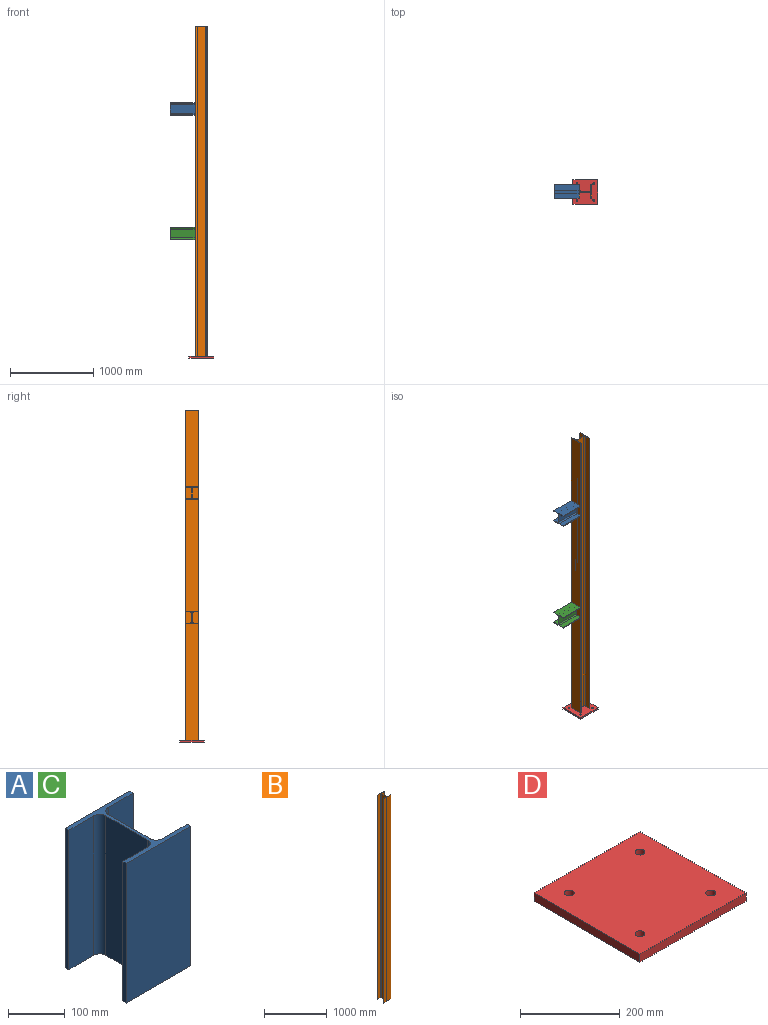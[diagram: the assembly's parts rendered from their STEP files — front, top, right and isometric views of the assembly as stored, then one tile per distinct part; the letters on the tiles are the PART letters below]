
ASSEMBLY  parts=4 mates=2
PART A: 18 faces, bbox 160x152x300 mm
  f0: plane 300x9mm, normal (-1,0,0), area 2700mm2, adj f1,f15,f16,f17
  f1: plane 300x62mm, normal (0,1,0), area 18600mm2, adj f0,f2,f16,f17
  f2: cylinder r=15mm len=300mm, axis (0,0,1), area 7068.6mm2, adj f1,f3,f16,f17
  f3: plane 300x104mm, normal (-1,0,0), area 31200mm2, adj f2,f4,f16,f17
  f4: cylinder r=15mm len=300mm, axis (0,0,1), area 7068.6mm2, adj f3,f5,f16,f17
  f5: plane 300x62mm, normal (0,-1,0), area 18600mm2, adj f4,f6,f16,f17
  f6: plane 300x9mm, normal (-1,0,0), area 2700mm2, adj f5,f7,f16,f17
  f7: plane 300x160mm, normal (0,1,0), area 48000mm2, adj f6,f8,f16,f17
  f8: plane 300x9mm, normal (1,0,0), area 2700mm2, adj f7,f9,f16,f17
  f9: plane 300x62mm, normal (0,-1,0), area 18600mm2, adj f8,f10,f16,f17
  f10: cylinder r=15mm len=300mm, axis (0,0,1), area 7068.6mm2, adj f9,f11,f16,f17
  f11: plane 300x104mm, normal (1,0,0), area 31200mm2, adj f10,f12,f16,f17
  f12: cylinder r=15mm len=300mm, axis (0,0,1), area 7068.6mm2, adj f11,f13,f16,f17
  f13: plane 300x62mm, normal (0,1,0), area 18600mm2, adj f12,f14,f16,f17
  f14: plane 300x9mm, normal (1,0,0), area 2700mm2, adj f13,f15,f16,f17
  f15: plane 300x160mm, normal (0,-1,0), area 48000mm2, adj f0,f14,f16,f17
  f16: plane 160x152mm, normal (0,0,1), area 3877.1mm2, adj f0,f1,f2,f3,f4,f5,f6,f7
  f17: plane 160x152mm, normal (0,0,-1), area 3877.1mm2, adj f0,f1,f2,f3,f4,f5,f6,f7
PART B: 18 faces, bbox 160x152x3980 mm
  f0: plane 3980x9mm, normal (-1,0,0), area 35820mm2, adj f1,f15,f16,f17
  f1: plane 3980x62mm, normal (0,1,0), area 246760mm2, adj f0,f2,f16,f17
  f2: cylinder r=15mm len=3980mm, axis (0,0,1), area 93776.5mm2, adj f1,f3,f16,f17
  f3: plane 3980x104mm, normal (-1,0,0), area 413920mm2, adj f2,f4,f16,f17
  f4: cylinder r=15mm len=3980mm, axis (0,0,1), area 93776.5mm2, adj f3,f5,f16,f17
  f5: plane 3980x62mm, normal (0,-1,0), area 246760mm2, adj f4,f6,f16,f17
  f6: plane 3980x9mm, normal (-1,0,0), area 35820mm2, adj f5,f7,f16,f17
  f7: plane 3980x160mm, normal (0,1,0), area 636800mm2, adj f6,f8,f16,f17
  f8: plane 3980x9mm, normal (1,0,0), area 35820mm2, adj f7,f9,f16,f17
  f9: plane 3980x62mm, normal (0,-1,0), area 246760mm2, adj f8,f10,f16,f17
  f10: cylinder r=15mm len=3980mm, axis (0,0,1), area 93776.5mm2, adj f9,f11,f16,f17
  f11: plane 3980x104mm, normal (1,0,0), area 413920mm2, adj f10,f12,f16,f17
  f12: cylinder r=15mm len=3980mm, axis (0,0,1), area 93776.5mm2, adj f11,f13,f16,f17
  f13: plane 3980x62mm, normal (0,1,0), area 246760mm2, adj f12,f14,f16,f17
  f14: plane 3980x9mm, normal (1,0,0), area 35820mm2, adj f13,f15,f16,f17
  f15: plane 3980x160mm, normal (0,-1,0), area 636800mm2, adj f0,f14,f16,f17
  f16: plane 160x152mm, normal (0,0,1), area 3877.1mm2, adj f0,f1,f2,f3,f4,f5,f6,f7
  f17: plane 160x152mm, normal (0,0,-1), area 3877.1mm2, adj f0,f1,f2,f3,f4,f5,f6,f7
PART C: same geometry as A
PART D: 10 faces, bbox 300x300x20 mm
  f0: plane 300x20mm, normal (1,0,0), area 6000mm2, adj f1,f6,f8,f9
  f1: plane 300x20mm, normal (0,1,0), area 6000mm2, adj f0,f2,f8,f9
  f2: plane 300x20mm, normal (-1,0,0), area 6000mm2, adj f1,f6,f8,f9
  f3: cylinder r=10mm len=20mm, axis (0,0,-1), area 1256.6mm2, adj f8,f9
  f4: cylinder r=10mm len=20mm, axis (0,0,-1), area 1256.6mm2, adj f8,f9
  f5: cylinder r=10mm len=20mm, axis (0,0,-1), area 1256.6mm2, adj f8,f9
  f6: plane 300x20mm, normal (0,-1,0), area 6000mm2, adj f0,f2,f8,f9
  f7: cylinder r=10mm len=20mm, axis (0,0,-1), area 1256.6mm2, adj f8,f9
  f8: plane 300x300mm, normal (0,0,1), area 88743.4mm2, adj f0,f1,f2,f3,f4,f5,f6,f7
  f9: plane 300x300mm, normal (0,0,-1), area 88743.4mm2, adj f0,f1,f2,f3,f4,f5,f6,f7
PLACE A rot(axis=(0.58,0.58,0.58),120deg) t=(-226,0,3000)mm
PLACE B rot(axis=(0,0,1),90deg) t=(0,0,2010)mm
PLACE C rot(axis=(0.58,0.58,0.58),120deg) t=(-226,0,1500)mm
PLACE D at identity
MATE fastened C.f16 <-> B.f7  axis (1,0,0) through (-76,0,1500)mm
MATE fastened B.f17 <-> D.f8  axis (0,0,-1) through (0,0,20)mm
